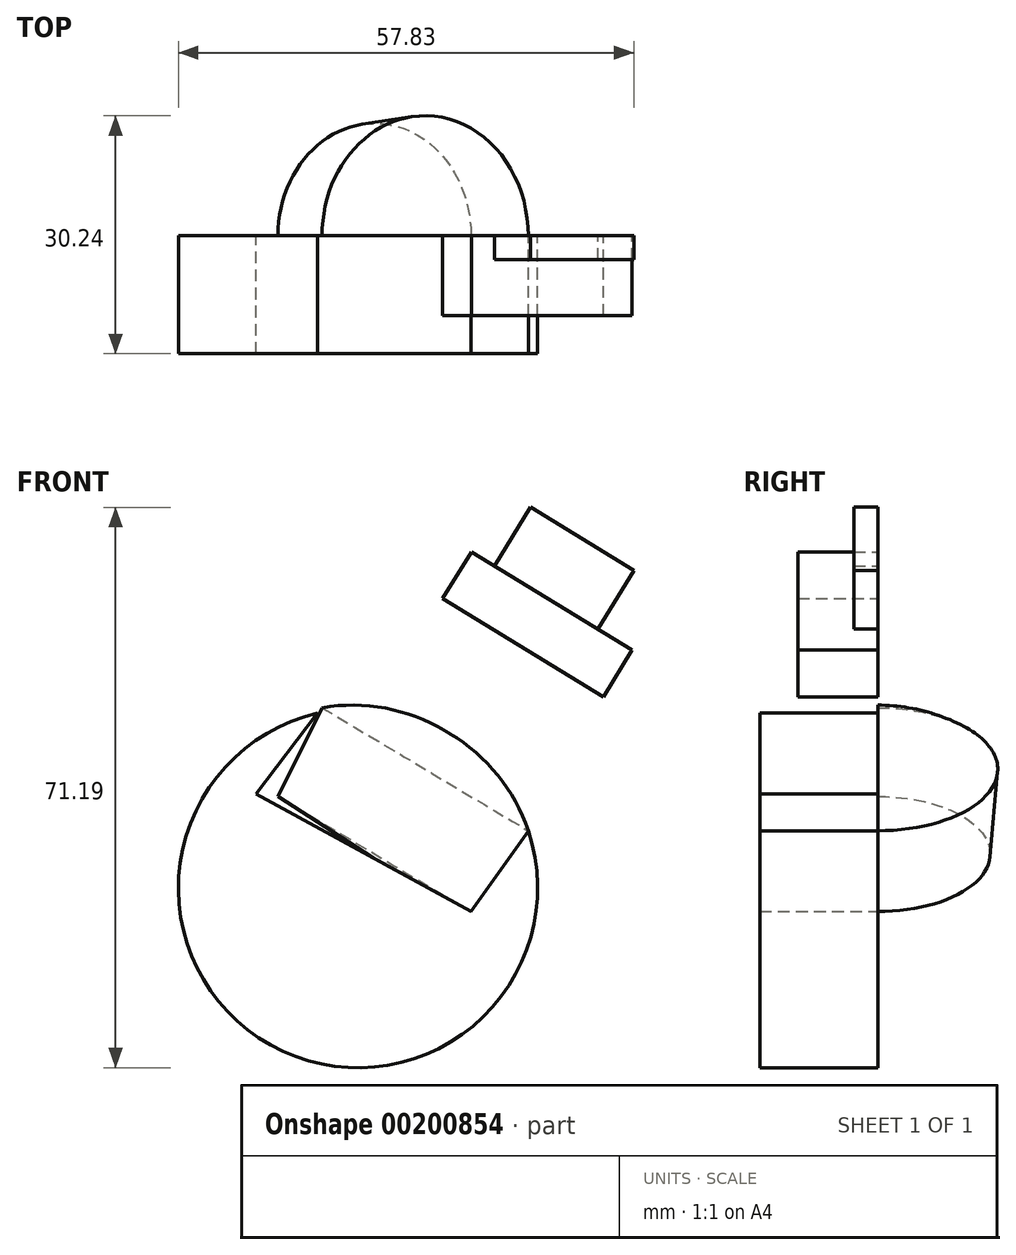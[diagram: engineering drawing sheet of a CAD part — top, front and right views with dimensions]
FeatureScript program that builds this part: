
annotation { "Feature Type Name" : "Feature", "Feature Type Description" : "" }
export const myFeature = defineFeature(function(context is Context, id is Id, definition is map)
    precondition{}
    {
        {
            var Q0;
            Q0=qCreatedBy(makeId("Front.planeOp"),FACE);
            var sketch = newSketch(context, id + "F0", { "sketchPlane" : qUnion([Q0])});
            skCircle(sketch, "E0", {"center": v(-3.78, -1.74) * mm, "radius": 22.81 * mm});
            skPoint(sketch, "E0.first.point", {"position": v(-22.66, 11.06) * mm});
            skPoint(sketch, "E0.second.point", {"position": v(14.56, -15.32) * mm});
            skPoint(sketch, "E0.third.point", {"position": v(0, -24.24) * mm});
            skLineSegment(sketch, "E1", {"start": v(3.7, 37.02) * mm, "end": v(-16.76, 10.23) * mm});
            skLineSegment(sketch, "E2", {"start": v(3.7, 37.02) * mm, "end": v(29.12, 21.5) * mm});
            skLineSegment(sketch, "E3", {"start": v(29.12, 21.5) * mm, "end": v(10.58, -4.74) * mm});
            skLineSegment(sketch, "E4", {"start": v(10.58, -4.74) * mm, "end": v(-16.76, 10.23) * mm});
            skLineSegment(sketch, "E5", {"start": v(31.04, 28.5) * mm, "end": v(27.4, 22.54) * mm});
            skLineSegment(sketch, "E6", {"start": v(31.04, 28.5) * mm, "end": v(10.62, 40.98) * mm});
            skLineSegment(sketch, "E7", {"start": v(10.62, 40.98) * mm, "end": v(6.98, 35.02) * mm});
            skLineSegment(sketch, "E8", {"start": v(18.13, 46.63) * mm, "end": v(13.57, 39.17) * mm});
            skLineSegment(sketch, "E9", {"start": v(18.13, 46.63) * mm, "end": v(31.24, 38.63) * mm});
            skLineSegment(sketch, "E10", {"start": v(31.24, 38.63) * mm, "end": v(26.68, 31.16) * mm});
            skLineSegment(sketch, "E11", {"start": v(7.55, 18.06) * mm, "end": v(-15.82, -21.12) * mm});
            skSolve(sketch);
        }
        {
            var Q0;
            {var subQ4=sQuery(id+"F0.wireOp",EDGE,"E0");var subQ6=makeQuery(id+"F0.imprint","INTERSECT",VERTEX,{"disambiguationData":[OD(0.0)],"derivedFrom":[subQ4,sQuery(id+"F0.wireOp",EDGE,"E11")]});Q0=makeQuery(id+"F0.imprint","IMPRINT",FACE,{"disambiguationData":[TD([[makeQuery(id+"F0.imprint","IMPRINT",EDGE,{"disambiguationData":[TD([[subQ6,1.0]])],"derivedFrom":subQ4}),-1.0]])]});}
            var Q1;
            {var subQ0=sQuery(id+"F0.wireOp",EDGE,"E11");var subQ1=sQuery(id+"F0.wireOp",EDGE,"E0");var subQ2=makeQuery(id+"F0.imprint","INTERSECT",VERTEX,{"disambiguationData":[OD(0.0)],"derivedFrom":[subQ1,subQ0]});Q1=makeQuery(id+"F0.imprint","IMPRINT",FACE,{"disambiguationData":[TD([[makeQuery(id+"F0.imprint","IMPRINT",EDGE,{"disambiguationData":[TD([[subQ2,1.0]])],"derivedFrom":subQ1}),1.0]])]});}
            var Q2;
            {var subQ0=sQuery(id+"F0.wireOp",EDGE,"E11");var subQ1=sQuery(id+"F0.wireOp",EDGE,"E0");var subQ2=makeQuery(id+"F0.imprint","INTERSECT",VERTEX,{"disambiguationData":[OD(0.0)],"derivedFrom":[subQ1,subQ0]});Q2=makeQuery(id+"F0.imprint","IMPRINT",FACE,{"disambiguationData":[TD([[makeQuery(id+"F0.imprint","IMPRINT",EDGE,{"disambiguationData":[TD([[subQ2,-1.0]])],"derivedFrom":subQ1}),1.0]])]});}
            extrude(context, id + "F1", {"entities" : qUnion([Q0, Q1, Q2]), "depth" : 15 * mm});
        }
        {
            var Q0;
            {var subQ3=sQuery(id+"F0.wireOp",EDGE,"E5");Q0=makeQuery(id+"F0.imprint","IMPRINT",FACE,{"disambiguationData":[TD([[makeQuery(id+"F0.imprint","IMPRINT",EDGE,{"derivedFrom":subQ3}),-1.0]])]});}
            extrude(context, id + "F2", {"entities" : qUnion([Q0]), "operationType" : NewBodyOperationType.ADD, "depth" : 10.16 * mm});
        }
        {
            var Q0;
            {var subQ0=sQuery(id+"F0.wireOp",EDGE,"E8");Q0=makeQuery(id+"F0.imprint","IMPRINT",FACE,{"disambiguationData":[TD([[makeQuery(id+"F0.imprint","IMPRINT",EDGE,{"derivedFrom":subQ0}),1.0]])]});}
            extrude(context, id + "F3", {"entities" : qUnion([Q0]), "operationType" : NewBodyOperationType.ADD, "depth" : 3.05 * mm});
        }
        {
            var Q0;
            {var subQ0=sQuery(id+"F0.wireOp",EDGE,"E11");var subQ1=sQuery(id+"F0.wireOp",EDGE,"E0");var subQ2=makeQuery(id+"F0.imprint","INTERSECT",VERTEX,{"disambiguationData":[OD(1.0)],"derivedFrom":[subQ1,subQ0]});Q0=makeQuery(id+"F0.imprint","IMPRINT",FACE,{"disambiguationData":[TD([[makeQuery(id+"F0.imprint","IMPRINT",EDGE,{"disambiguationData":[TD([[subQ2,1.0]])],"derivedFrom":subQ1}),1.0]])]});}
            var Q1;
            Q1=sQuery(id+"F0.wireOp",EDGE,"E11");
            revolve(context, id + "F4", {"entities" : qUnion([Q0]), "axis" : qUnion([Q1]), "revolveType" : RevolveType.ONE_DIRECTION, "oppositeDirection" : true, "angle" : 180 * degree});
        }
    });
